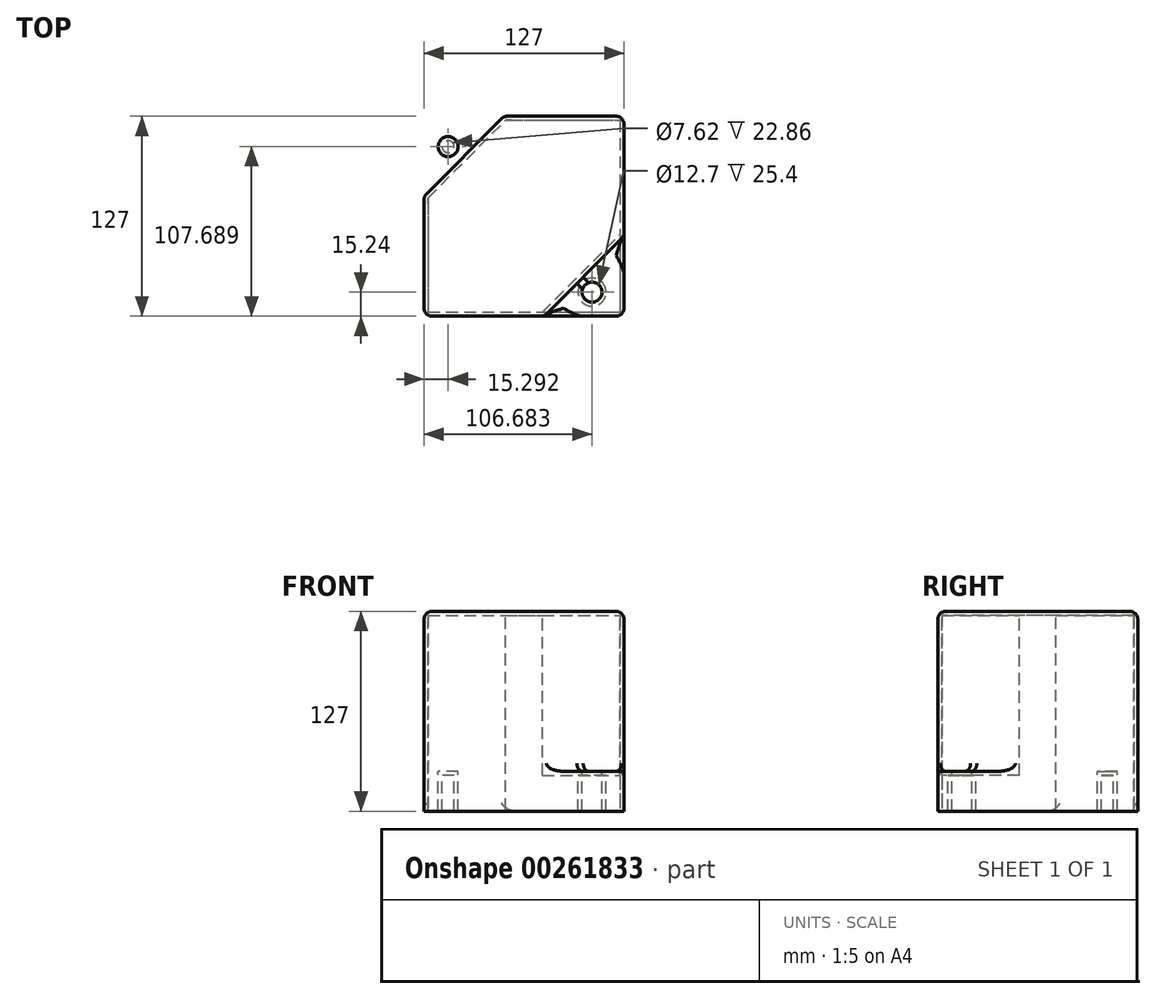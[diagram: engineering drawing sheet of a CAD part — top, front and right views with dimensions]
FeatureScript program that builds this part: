
annotation { "Feature Type Name" : "Feature", "Feature Type Description" : "" }
export const myFeature = defineFeature(function(context is Context, id is Id, definition is map)
    precondition{}
    {
        {
            var Q0;
            Q0=qCreatedBy(makeId("Top.planeOp"),FACE);
            var sketch = newSketch(context, id + "F0", { "sketchPlane" : qUnion([Q0])});
            skLineSegment(sketch, "E0.bottom", {"start": v(-68.54, 81.1) * mm, "end": v(58.46, 81.1) * mm});
            skLineSegment(sketch, "E0.top", {"start": v(-68.54, -45.9) * mm, "end": v(58.46, -45.9) * mm});
            skLineSegment(sketch, "E0.left", {"start": v(-68.54, 81.1) * mm, "end": v(-68.54, -45.9) * mm});
            skLineSegment(sketch, "E0.right", {"start": v(58.46, 81.1) * mm, "end": v(58.46, -45.9) * mm});
            skSolve(sketch);
        }
        {
            var Q0;
            Q0 = qSketchRegion(id + "F0", true);
            extrude(context, id + "F1", {"entities" : qUnion([Q0]), "depth" : 127 * mm});
        }
        {
            var Q0;
            Q0=makeQuery(id+"F1.opExtrude","CAP_FACE",FACE,{"disambiguationData":[OSD([sQuery(id+"F0.wireOp",EDGE,"E0.bottom"),sQuery(id+"F0.wireOp",EDGE,"E0.top"),sQuery(id+"F0.wireOp",EDGE,"E0.left"),sQuery(id+"F0.wireOp",EDGE,"E0.right")])],"isStart":false});
            var sketch = newSketch(context, id + "F2", { "sketchPlane" : qUnion([Q0])});
            skLineSegment(sketch, "E1", {"start": v(-68.54, 81.1) * mm, "end": v(-68.54, 30.3) * mm});
            skLineSegment(sketch, "E2", {"start": v(-68.54, 30.3) * mm, "end": v(-17.74, 81.1) * mm});
            skLineSegment(sketch, "E3", {"start": v(-17.74, 81.1) * mm, "end": v(-68.54, 81.1) * mm});
            skLineSegment(sketch, "E4", {"start": v(-68.54, -45.9) * mm, "end": v(58.46, 81.1) * mm, "construction": true});
            skLineSegment(sketch, "E5.MirrorCS", {"start": v(7.66, -45.9) * mm, "end": v(58.46, 4.9) * mm});
            skLineSegment(sketch, "E6.MirrorCS", {"start": v(58.46, -45.9) * mm, "end": v(7.66, -45.9) * mm});
            skLineSegment(sketch, "E7.MirrorCS", {"start": v(58.46, 4.9) * mm, "end": v(58.46, -45.9) * mm});
            skSolve(sketch);
        }
        {
            var Q0;
            Q0=makeQuery(id+"F2.imprint","IMPRINT",FACE,{"disambiguationData":[TD([[makeQuery(id+"F2.imprint","IMPRINT",EDGE,{"derivedFrom":sQuery(id+"F2.wireOp",EDGE,"E5.MirrorCS")}),-1.0]])]});
            var Q1;
            Q1=makeQuery(id+"F2.imprint","IMPRINT",FACE,{"disambiguationData":[TD([[makeQuery(id+"F2.imprint","IMPRINT",EDGE,{"derivedFrom":sQuery(id+"F2.wireOp",EDGE,"E1")}),1.0]])]});
            extrude(context, id + "F3", {"entities" : qUnion([Q0, Q1]), "operationType" : NewBodyOperationType.REMOVE, "oppositeDirection" : true, "depth" : 101.6 * mm});
        }
        {
            var Q0;
            Q0=makeQuery(id+"F3.boolean.opBoolean","COPY",FACE,{"derivedFrom":makeQuery(id+"F3.opExtrude","CAP_FACE",FACE,{"disambiguationData":[OSD([sQuery(id+"F2.wireOp",EDGE,"E1"),sQuery(id+"F2.wireOp",EDGE,"E2"),sQuery(id+"F2.wireOp",EDGE,"E3")])],"isStart":false})});
            var sketch = newSketch(context, id + "F4", { "sketchPlane" : qUnion([Q0])});
            skCircle(sketch, "E8", {"center": v(38.14, -30.65) * mm, "radius": 6.35 * mm});
            skLineSegment(sketch, "E9", {"start": v(-68.99, -45.15) * mm, "end": v(58.3, 80.67) * mm, "construction": true});
            skCircle(sketch, "E10.MirrorC", {"center": v(-53.25, 61.8) * mm, "radius": 6.35 * mm});
            skSolve(sketch);
        }
        {
            var Q0;
            Q0=makeQuery(id+"F4.imprint","IMPRINT",FACE,{"disambiguationData":[TD([[makeQuery(id+"F4.imprint","IMPRINT",EDGE,{"derivedFrom":sQuery(id+"F4.wireOp",EDGE,"E10.MirrorC")}),-1.0]])]});
            var Q1;
            Q1=makeQuery(id+"F4.imprint","IMPRINT",FACE,{"disambiguationData":[TD([[makeQuery(id+"F4.imprint","IMPRINT",EDGE,{"derivedFrom":sQuery(id+"F4.wireOp",EDGE,"E8")}),1.0]])]});
            extrude(context, id + "F5", {"entities" : qUnion([Q0, Q1]), "operationType" : NewBodyOperationType.REMOVE, "oppositeDirection" : true, "depth" : 203.2 * mm});
        }
        {
            var Q0;
            Q0=makeQuery(id+"F1.opExtrude","CAP_FACE",FACE,{"disambiguationData":[OSD([sQuery(id+"F0.wireOp",EDGE,"E0.bottom"),sQuery(id+"F0.wireOp",EDGE,"E0.top"),sQuery(id+"F0.wireOp",EDGE,"E0.left"),sQuery(id+"F0.wireOp",EDGE,"E0.right")])],"isStart":true});
            shell(context, id + "F6", {"entities" : qUnion([Q0]), "thickness" : 2.54 * mm});
        }
        {
            var Q0;
            Q0=makeQuery(id+"F1.opExtrude","CAP_EDGE",EDGE,{"disambiguationData":[OSD([sQuery(id+"F0.wireOp",EDGE,"E0.top")])],"isStart":false});
            var Q1;
            Q1=makeQuery(id+"F3.boolean.opBoolean","COPY",EDGE,{"derivedFrom":makeQuery(id+"F3.opExtrude","CAP_EDGE",EDGE,{"disambiguationData":[OSD([sQuery(id+"F2.wireOp",EDGE,"E5.MirrorCS")])],"isStart":true})});
            var Q2;
            Q2=makeQuery(id+"F1.opExtrude","CAP_EDGE",EDGE,{"disambiguationData":[OSD([sQuery(id+"F0.wireOp",EDGE,"E0.right")])],"isStart":false});
            var Q3;
            Q3=makeQuery(id+"F1.opExtrude","CAP_EDGE",EDGE,{"disambiguationData":[OSD([sQuery(id+"F0.wireOp",EDGE,"E0.bottom")])],"isStart":false});
            var Q4;
            Q4=makeQuery(id+"F3.boolean.opBoolean","COPY",EDGE,{"derivedFrom":makeQuery(id+"F3.opExtrude","CAP_EDGE",EDGE,{"disambiguationData":[OSD([sQuery(id+"F2.wireOp",EDGE,"E2")])],"isStart":true})});
            var Q5;
            Q5=makeQuery(id+"F1.opExtrude","CAP_EDGE",EDGE,{"disambiguationData":[OSD([sQuery(id+"F0.wireOp",EDGE,"E0.left")])],"isStart":false});
            var Q6;
            Q6=makeQuery(id+"F3.boolean.opBoolean","COPY",EDGE,{"derivedFrom":makeQuery(id+"F3.opExtrude","SWEPT_EDGE",EDGE,{"disambiguationData":[OSD([sQuery(id+"F0.wireOp",EDGE,"E0.top"),sQuery(id+"F2.wireOp",EDGE,"E5.MirrorCS"),sQuery(id+"F2.wireOp",EDGE,"E6.MirrorCS")])]})});
            var Q7;
            Q7=makeQuery(id+"F3.boolean.opBoolean","COPY",EDGE,{"derivedFrom":makeQuery(id+"F3.opExtrude","SWEPT_EDGE",EDGE,{"disambiguationData":[OSD([sQuery(id+"F0.wireOp",EDGE,"E0.right"),sQuery(id+"F2.wireOp",EDGE,"E5.MirrorCS"),sQuery(id+"F2.wireOp",EDGE,"E7.MirrorCS")])]})});
            var Q8;
            Q8=makeQuery(id+"F3.boolean.opBoolean","COPY",EDGE,{"derivedFrom":makeQuery(id+"F3.opExtrude","CAP_EDGE",EDGE,{"disambiguationData":[OSD([sQuery(id+"F2.wireOp",EDGE,"E7.MirrorCS")])],"isStart":false})});
            var Q9;
            Q9=makeQuery(id+"F3.boolean.opBoolean","COPY",EDGE,{"derivedFrom":makeQuery(id+"F3.opExtrude","CAP_EDGE",EDGE,{"disambiguationData":[OSD([sQuery(id+"F2.wireOp",EDGE,"E6.MirrorCS")])],"isStart":false})});
            var Q10;
            Q10=makeQuery(id+"F1.opExtrude","SWEPT_EDGE",EDGE,{"disambiguationData":[OSD([sQuery(id+"F0.wireOp",EDGE,"E0.top"),sQuery(id+"F0.wireOp",EDGE,"E0.right")])]});
            var Q11;
            Q11=makeQuery(id+"F1.opExtrude","SWEPT_EDGE",EDGE,{"disambiguationData":[OSD([sQuery(id+"F0.wireOp",EDGE,"E0.top"),sQuery(id+"F0.wireOp",EDGE,"E0.left")])]});
            var Q12;
            Q12=makeQuery(id+"F3.boolean.opBoolean","COPY",EDGE,{"derivedFrom":makeQuery(id+"F3.opExtrude","SWEPT_EDGE",EDGE,{"disambiguationData":[OSD([sQuery(id+"F0.wireOp",EDGE,"E0.left"),sQuery(id+"F2.wireOp",EDGE,"E1"),sQuery(id+"F2.wireOp",EDGE,"E2")])]})});
            var Q13;
            Q13=makeQuery(id+"F3.boolean.opBoolean","COPY",FACE,{"derivedFrom":makeQuery(id+"F3.opExtrude","SWEPT_FACE",FACE,{"disambiguationData":[OSD([sQuery(id+"F2.wireOp",EDGE,"E2")])]})});
            var Q14;
            Q14=makeQuery(id+"F3.boolean.opBoolean","COPY",EDGE,{"derivedFrom":makeQuery(id+"F3.opExtrude","SWEPT_EDGE",EDGE,{"disambiguationData":[OSD([sQuery(id+"F0.wireOp",EDGE,"E0.bottom"),sQuery(id+"F2.wireOp",EDGE,"E2"),sQuery(id+"F2.wireOp",EDGE,"E3")])]})});
            var Q15;
            Q15=makeQuery(id+"F3.boolean.opBoolean","COPY",EDGE,{"derivedFrom":makeQuery(id+"F3.opExtrude","CAP_EDGE",EDGE,{"disambiguationData":[OSD([sQuery(id+"F2.wireOp",EDGE,"E1")])],"isStart":false})});
            var Q16;
            Q16=makeQuery(id+"F3.boolean.opBoolean","COPY",EDGE,{"derivedFrom":makeQuery(id+"F3.opExtrude","CAP_EDGE",EDGE,{"disambiguationData":[OSD([sQuery(id+"F2.wireOp",EDGE,"E3")])],"isStart":false})});
            var Q17;
            Q17=makeQuery(id+"F3.boolean.opBoolean","COPY",FACE,{"derivedFrom":makeQuery(id+"F3.opExtrude","SWEPT_FACE",FACE,{"disambiguationData":[OSD([sQuery(id+"F2.wireOp",EDGE,"E5.MirrorCS")])]})});
            var Q18;
            Q18=makeQuery(id+"F1.opExtrude","SWEPT_EDGE",EDGE,{"disambiguationData":[OSD([sQuery(id+"F0.wireOp",EDGE,"E0.bottom"),sQuery(id+"F0.wireOp",EDGE,"E0.right")])]});
            fillet(context, id + "F7", {"entities" : qUnion([Q0, Q1, Q2, Q3, Q4, Q5, Q6, Q7, Q8, Q9, Q10, Q11, Q12, Q13, Q14, Q15, Q16, Q17, Q18]), "radius" : 5.08 * mm, "tangentPropagation" : true, "allowEdgeOverflow" : false});
        }
    });
